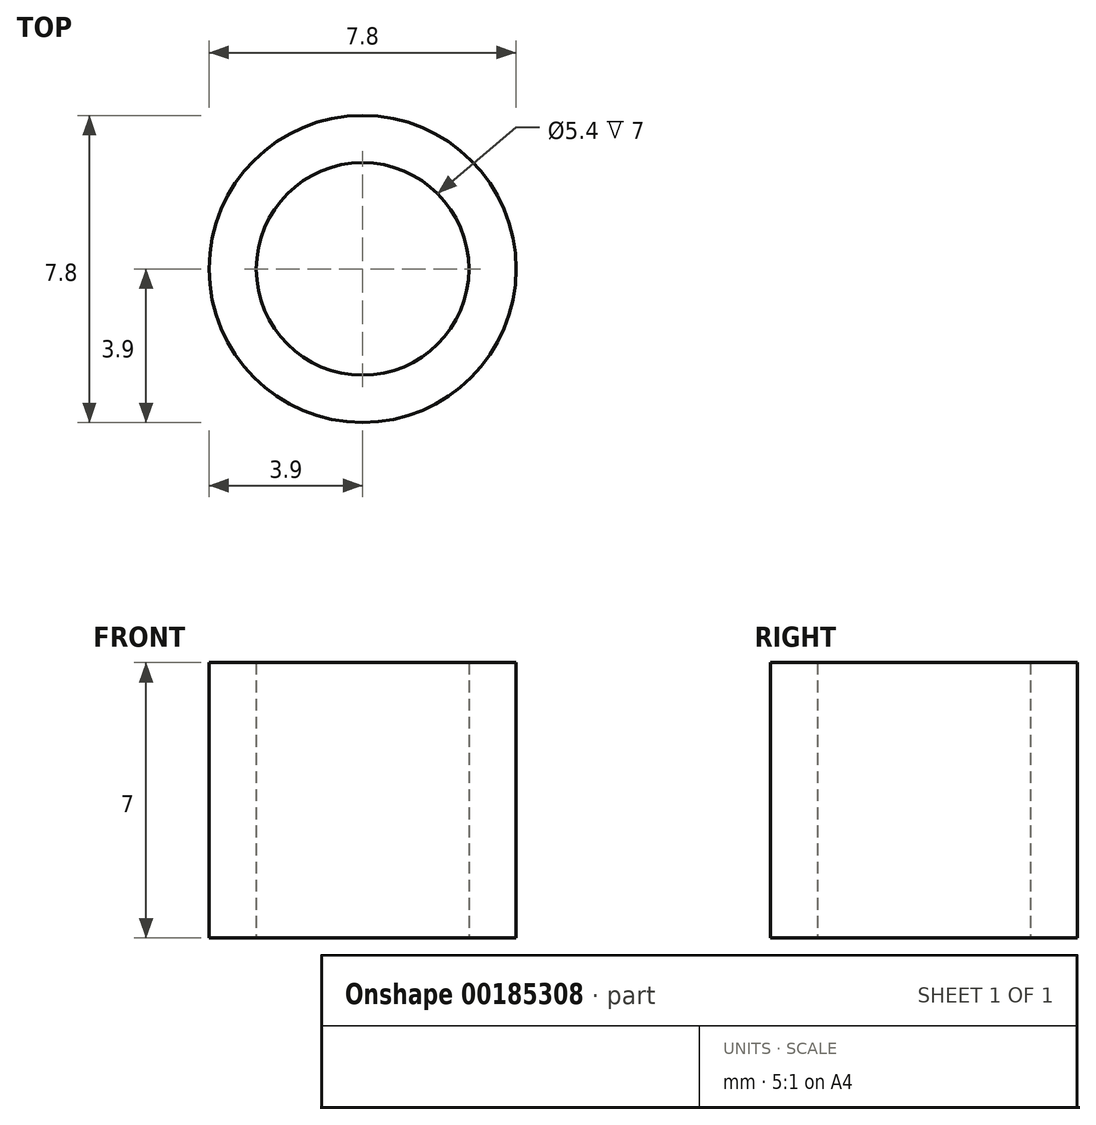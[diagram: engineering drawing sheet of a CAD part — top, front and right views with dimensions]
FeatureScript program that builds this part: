
annotation { "Feature Type Name" : "Feature", "Feature Type Description" : "" }
export const myFeature = defineFeature(function(context is Context, id is Id, definition is map)
    precondition{}
    {
        {
            var Q0;
            Q0=qCreatedBy(makeId("Top.planeOp"),FACE);
            var sketch = newSketch(context, id + "F0", { "sketchPlane" : qUnion([Q0])});
            skCircle(sketch, "E0", {"center": v(0, 0) * mm, "radius": 2.7 * mm});
            skCircle(sketch, "E1", {"center": v(0, 0) * mm, "radius": 3.9 * mm});
            skSolve(sketch);
        }
        {
            var Q0;
            Q0 = qSketchRegion(id + "F0", true);
            extrude(context, id + "F1", {"entities" : qUnion([Q0]), "depth" : 7 * mm});
        }
    });
